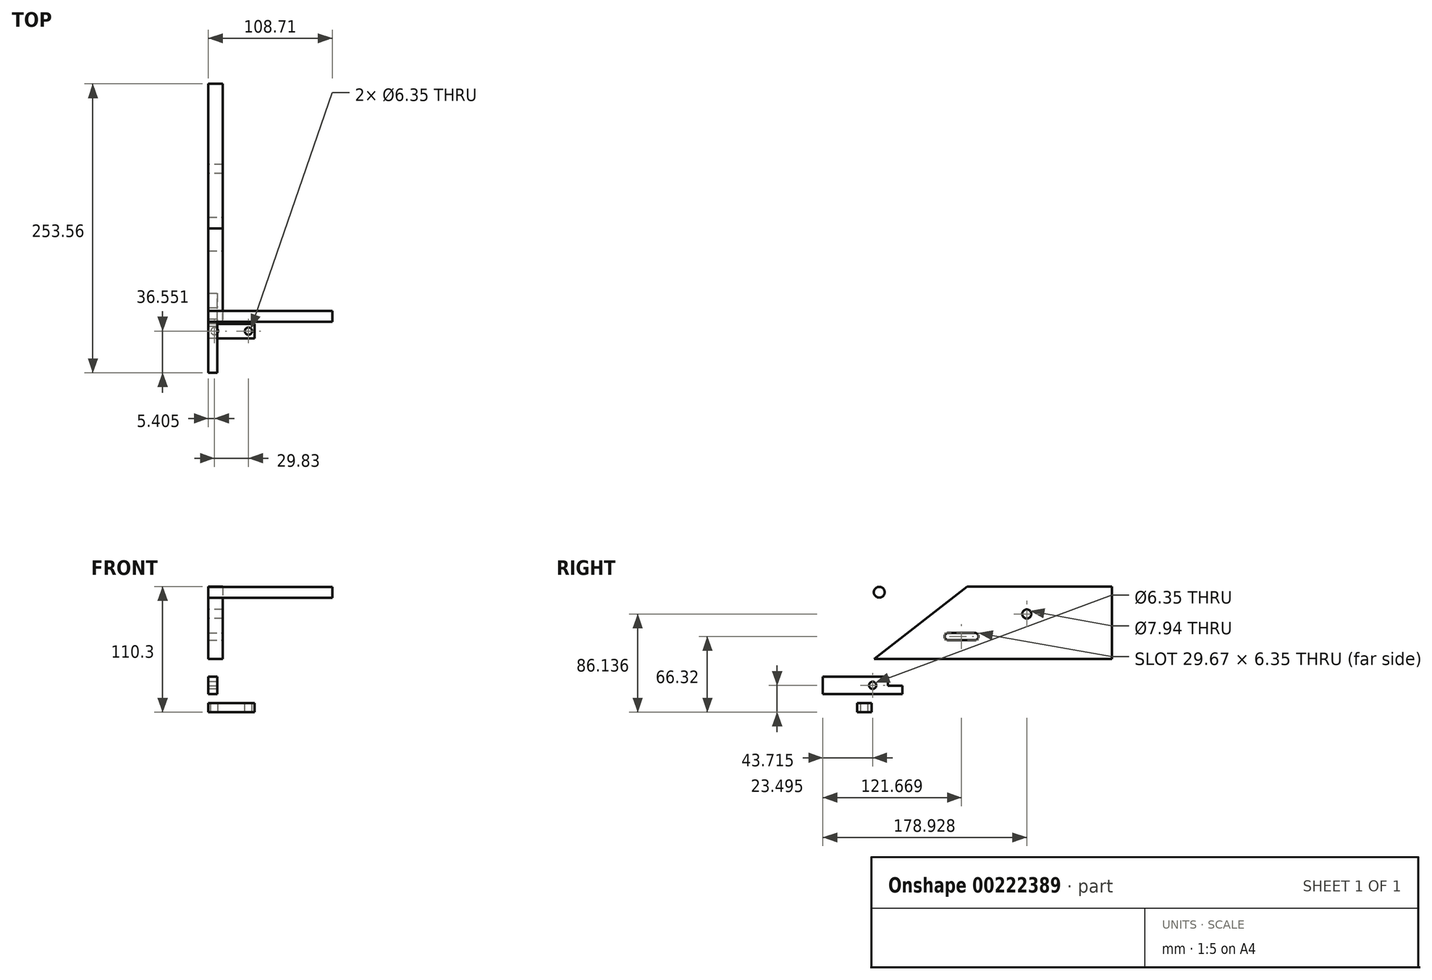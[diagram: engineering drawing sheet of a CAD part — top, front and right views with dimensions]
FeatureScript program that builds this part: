
annotation { "Feature Type Name" : "Feature", "Feature Type Description" : "" }
export const myFeature = defineFeature(function(context is Context, id is Id, definition is map)
    precondition{}
    {
        {
            var Q0;
            Q0=qCreatedBy(makeId("Right.planeOp"),FACE);
            var sketch = newSketch(context, id + "F0", { "sketchPlane" : qUnion([Q0])});
            skLineSegment(sketch, "E0", {"start": v(-54.38, -19.52) * mm, "end": v(154.15, -19.52) * mm});
            skLineSegment(sketch, "E1", {"start": v(154.15, -19.52) * mm, "end": v(154.15, 43.98) * mm});
            skLineSegment(sketch, "E2", {"start": v(154.15, 43.98) * mm, "end": v(27.15, 43.98) * mm});
            skLineSegment(sketch, "E3", {"start": v(27.15, 43.98) * mm, "end": v(-54.38, -19.52) * mm});
            skCircle(sketch, "E4", {"center": v(79.52, 19.82) * mm, "radius": 3.97 * mm});
            skSolve(sketch);
        }
        {
            var Q0;
            Q0 = qSketchRegion(id + "F0", true);
            extrude(context, id + "F1", {"entities" : qUnion([Q0]), "depth" : 12.7 * mm});
        }
        {
            var Q0;
            Q0=qCreatedBy(makeId("Right.planeOp"),FACE);
            var sketch = newSketch(context, id + "F2", { "sketchPlane" : qUnion([Q0])});
            skLineSegment(sketch, "E5.bottom", {"start": v(-25.42, -41.98) * mm, "end": v(76.18, -41.98) * mm});
            skLineSegment(sketch, "E5.top", {"start": v(-25.42, -49.91) * mm, "end": v(76.18, -49.91) * mm});
            skLineSegment(sketch, "E5.left", {"start": v(-25.42, -41.98) * mm, "end": v(-25.42, -49.91) * mm});
            skLineSegment(sketch, "E5.right", {"start": v(76.18, -41.98) * mm, "end": v(76.18, -49.91) * mm});
            skSolve(sketch);
        }
        {
            var Q0;
            Q0 = qSketchRegion(id + "F2", true);
            extrude(context, id + "F3", {"entities" : qUnion([Q0]), "depth" : 42.42 * mm});
        }
        {
            var Q0;
            Q0=qCreatedBy(makeId("Right.planeOp"),FACE);
            var sketch = newSketch(context, id + "F4", { "sketchPlane" : qUnion([Q0])});
            skCircle(sketch, "E6", {"center": v(-49.9, 38.87) * mm, "radius": 4.76 * mm});
            skSolve(sketch);
        }
        {
            var Q0;
            Q0 = qSketchRegion(id + "F4", true);
            extrude(context, id + "F5", {"entities" : qUnion([Q0]), "depth" : 108.7 * mm});
        }
        {
            var Q0;
            Q0=makeQuery(id+"F1.opExtrude","CAP_FACE",FACE,{"disambiguationData":[OSD([sQuery(id+"F0.wireOp",EDGE,"E0"),sQuery(id+"F0.wireOp",EDGE,"E1"),sQuery(id+"F0.wireOp",EDGE,"E2"),sQuery(id+"F0.wireOp",EDGE,"E3"),sQuery(id+"F0.wireOp",EDGE,"E4")])],"isStart":false});
            var sketch = newSketch(context, id + "F6", { "sketchPlane" : qUnion([Q0])});
            skLineSegment(sketch, "E7", {"start": v(10.6, 3.18) * mm, "end": v(33.92, 3.18) * mm});
            skLineSegment(sketch, "E8", {"start": v(10.6, -3.18) * mm, "end": v(33.92, -3.18) * mm});
            skArc(sketch, "E9", {"start": v(33.92, -3.18) * mm, "mid": v(37.1, 0) * mm, "end": v(33.92, 3.18) * mm});
            skArc(sketch, "E10", {"start": v(10.6, 3.18) * mm, "mid": v(7.42, 0) * mm, "end": v(10.6, -3.18) * mm});
            skSolve(sketch);
        }
        {
            var Q0;
            Q0 = qSketchRegion(id + "F6", true);
            var Q1;
            Q1=makeQuery(id+"F1.opExtrude","CAP_FACE",FACE,{"disambiguationData":[OSD([sQuery(id+"F0.wireOp",EDGE,"E0"),sQuery(id+"F0.wireOp",EDGE,"E1"),sQuery(id+"F0.wireOp",EDGE,"E2"),sQuery(id+"F0.wireOp",EDGE,"E3"),sQuery(id+"F0.wireOp",EDGE,"E4")])],"isStart":true});
            extrude(context, id + "F7", {"entities" : qUnion([Q0]), "operationType" : NewBodyOperationType.REMOVE, "endBound" : BoundingType.UP_TO_SURFACE, "oppositeDirection" : true, "endBoundEntityFace" : qUnion([Q1]), "depth" : 25.4 * mm});
        }
        {
            var Q0;
            Q0=makeQuery(id+"F3.opExtrude","SWEPT_BODY",BODY,{"disambiguationData":[OSD([sQuery(id+"F2.wireOp",EDGE,"E5.bottom"),sQuery(id+"F2.wireOp",EDGE,"E5.top"),sQuery(id+"F2.wireOp",EDGE,"E5.left"),sQuery(id+"F2.wireOp",EDGE,"E5.right")])]});
            deleteBodies(context, id + "F8", {"entities" : qUnion([Q0])});
        }
        {
            var Q0;
            Q0=qCreatedBy(makeId("Right.planeOp"),FACE);
            var sketch = newSketch(context, id + "F9", { "sketchPlane" : qUnion([Q0])});
            skLineSegment(sketch, "E11.bottom", {"start": v(-99.41, -35.2) * mm, "end": v(-35.91, -35.2) * mm});
            skLineSegment(sketch, "E11.top", {"start": v(-99.41, -50.45) * mm, "end": v(-35.91, -50.45) * mm});
            skLineSegment(sketch, "E11.left", {"start": v(-99.41, -35.2) * mm, "end": v(-99.41, -50.45) * mm});
            skLineSegment(sketch, "E11.right", {"start": v(-35.91, -35.2) * mm, "end": v(-35.91, -50.45) * mm});
            skLineSegment(sketch, "E12", {"start": v(-29.56, -35.2) * mm, "end": v(-35.91, -35.2) * mm});
            skCircle(sketch, "E13", {"center": v(-55.7, -42.83) * mm, "radius": 3.18 * mm});
            skPoint(sketch, "E13.centerSnap0", {"position": v(-99.41, -42.83) * mm});
            skLineSegment(sketch, "E14", {"start": v(-29.56, -35.2) * mm, "end": v(-29.56, -50.45) * mm});
            skLineSegment(sketch, "E15", {"start": v(-29.56, -50.45) * mm, "end": v(-35.91, -50.45) * mm});
            skSolve(sketch);
        }
        {
            var Q0;
            Q0=makeQuery(id+"F9.imprint","IMPRINT",FACE,{"disambiguationData":[TD([[makeQuery(id+"F9.imprint","IMPRINT",EDGE,{"derivedFrom":sQuery(id+"F9.wireOp",EDGE,"E11.bottom")}),-1.0]])]});
            var Q1;
            Q1=makeQuery(id+"F9.imprint","IMPRINT",FACE,{"disambiguationData":[TD([[makeQuery(id+"F9.imprint","IMPRINT",EDGE,{"derivedFrom":sQuery(id+"F9.wireOp",EDGE,"E11.right")}),1.0]])]});
            extrude(context, id + "F10", {"entities" : qUnion([Q0, Q1]), "depth" : 7.94 * mm});
        }
        {
            var Q0;
            Q0=qCreatedBy(makeId("Right.planeOp"),FACE);
            var sketch = newSketch(context, id + "F11", { "sketchPlane" : qUnion([Q0])});
            skLineSegment(sketch, "E16.bottom", {"start": v(-69.2, -58.37) * mm, "end": v(-56.5, -58.37) * mm});
            skLineSegment(sketch, "E16.top", {"start": v(-69.2, -66.32) * mm, "end": v(-56.5, -66.32) * mm});
            skLineSegment(sketch, "E16.left", {"start": v(-69.2, -58.37) * mm, "end": v(-69.2, -66.32) * mm});
            skLineSegment(sketch, "E16.right", {"start": v(-56.5, -58.37) * mm, "end": v(-56.5, -66.32) * mm});
            skSolve(sketch);
        }
        {
            var Q0;
            Q0 = qSketchRegion(id + "F11", true);
            extrude(context, id + "F12", {"entities" : qUnion([Q0]), "depth" : 40.64 * mm});
        }
        {
            var Q0;
            Q0=makeQuery(id+"F10.opExtrude","CAP_FACE",FACE,{"disambiguationData":[OSD([sQuery(id+"F9.wireOp",EDGE,"E11.bottom"),sQuery(id+"F9.wireOp",EDGE,"E11.top"),sQuery(id+"F9.wireOp",EDGE,"E11.left"),sQuery(id+"F9.wireOp",EDGE,"E12"),sQuery(id+"F9.wireOp",EDGE,"yvIYH8AZ-Si4f-MHAU-ZJ0y-jJaww5wwn13a"),sQuery(id+"F9.wireOp",EDGE,"E13")])],"isStart":false});
            var sketch = newSketch(context, id + "F13", { "sketchPlane" : qUnion([Q0])});
            skLineSegment(sketch, "E17.bottom", {"start": v(-29.56, -35.2) * mm, "end": v(-42.26, -35.2) * mm});
            skLineSegment(sketch, "E17.top", {"start": v(-29.56, -43.16) * mm, "end": v(-42.26, -43.16) * mm});
            skLineSegment(sketch, "E17.left", {"start": v(-29.56, -35.2) * mm, "end": v(-29.56, -43.16) * mm});
            skLineSegment(sketch, "E17.right", {"start": v(-42.26, -35.2) * mm, "end": v(-42.26, -43.16) * mm});
            skSolve(sketch);
        }
        {
            var Q0;
            Q0 = qSketchRegion(id + "F13", true);
            extrude(context, id + "F14", {"entities" : qUnion([Q0]), "operationType" : NewBodyOperationType.REMOVE, "endBound" : BoundingType.THROUGH_ALL, "oppositeDirection" : true, "depth" : 25.4 * mm});
        }
        {
            var Q0;
            Q0=makeQuery(id+"F12.opExtrude","SWEPT_FACE",FACE,{"disambiguationData":[OSD([sQuery(id+"F11.wireOp",EDGE,"E16.bottom")])]});
            var sketch = newSketch(context, id + "F15", { "sketchPlane" : qUnion([Q0])});
            skCircle(sketch, "E18", {"center": v(35.24, -62.86) * mm, "radius": 3.18 * mm});
            skPoint(sketch, "E18.centerSnap0", {"position": v(40.64, -62.86) * mm});
            skLineSegment(sketch, "E19", {"start": v(20.32, -69.2) * mm, "end": v(20.32, -63.88) * mm});
            skCircle(sketch, "E20.MirrorC", {"center": v(5.4, -62.86) * mm, "radius": 3.18 * mm});
            skSolve(sketch);
        }
        {
            var Q0;
            Q0 = qSketchRegion(id + "F15", true);
            extrude(context, id + "F16", {"entities" : qUnion([Q0]), "operationType" : NewBodyOperationType.REMOVE, "endBound" : BoundingType.THROUGH_ALL, "oppositeDirection" : true, "depth" : 25.4 * mm});
        }
    });
